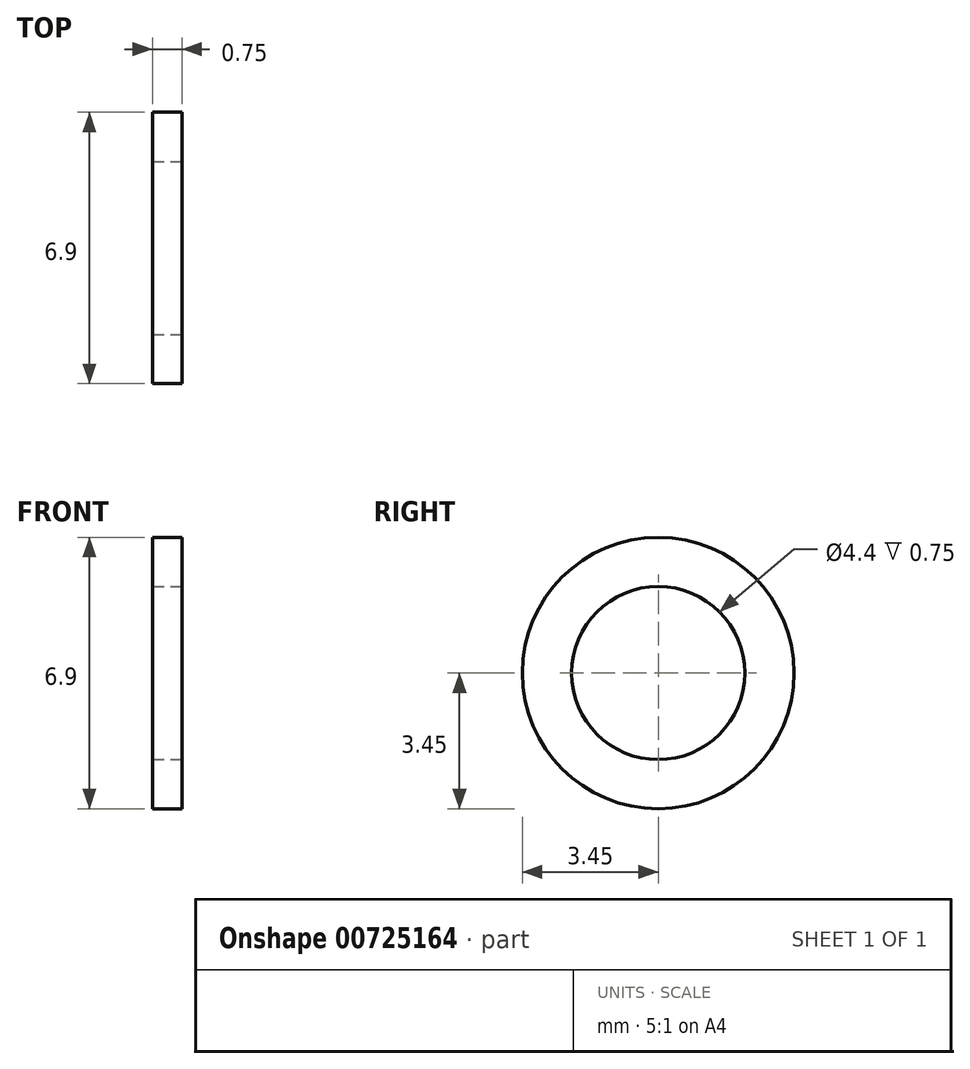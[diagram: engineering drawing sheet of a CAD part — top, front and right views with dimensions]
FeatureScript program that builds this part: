
annotation { "Feature Type Name" : "Feature", "Feature Type Description" : "" }
export const myFeature = defineFeature(function(context is Context, id is Id, definition is map)
    precondition{}
    {
        {
            var Q0;
            Q0=qCreatedBy(makeId("Right.planeOp"),FACE);
            var sketch = newSketch(context, id + "F0", { "sketchPlane" : qUnion([Q0])});
            skCircle(sketch, "E0", {"center": v(0, 0) * mm, "radius": 3.45 * mm});
            skSolve(sketch);
        }
        {
            var Q0;
            Q0 = qSketchRegion(id + "F0", true);
            extrude(context, id + "F1", {"entities" : qUnion([Q0]), "depth" : 0.75 * mm, "offsetDistance" : 25 * mm});
        }
        {
            var Q0;
            Q0=makeQuery(id+"F1.opExtrude","CAP_FACE",FACE,{"disambiguationData":[OSD([sQuery(id+"F0.wireOp",EDGE,"E0")])],"isStart":false});
            var sketch = newSketch(context, id + "F2", { "sketchPlane" : qUnion([Q0])});
            skCircle(sketch, "E1", {"center": v(0, 0) * mm, "radius": 2.2 * mm});
            skSolve(sketch);
        }
        {
            var Q0;
            Q0 = qSketchRegion(id + "F2", true);
            extrude(context, id + "F3", {"entities" : qUnion([Q0]), "operationType" : NewBodyOperationType.REMOVE, "oppositeDirection" : true, "depth" : 2 * mm, "offsetDistance" : 25 * mm});
        }
    });
